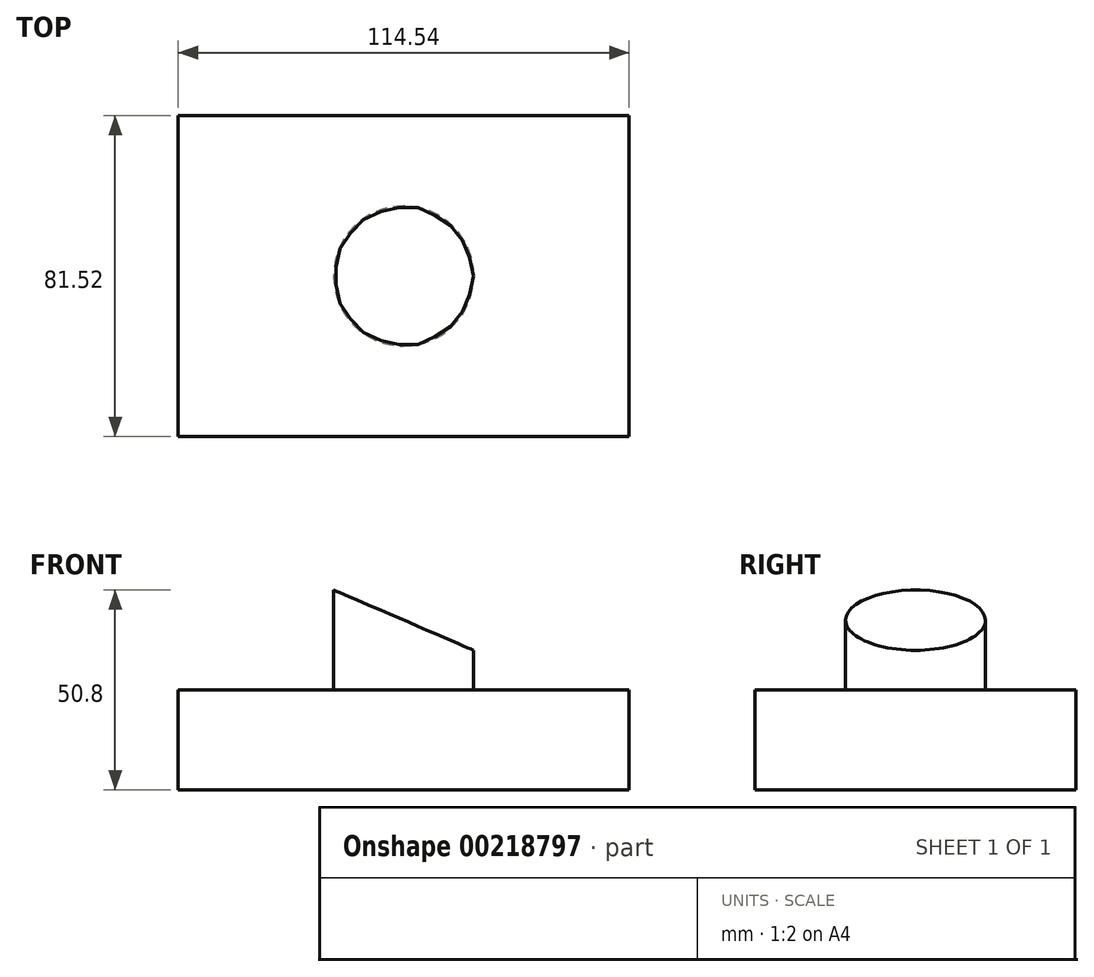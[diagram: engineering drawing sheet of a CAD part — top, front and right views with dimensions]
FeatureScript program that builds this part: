
annotation { "Feature Type Name" : "Feature", "Feature Type Description" : "" }
export const myFeature = defineFeature(function(context is Context, id is Id, definition is map)
    precondition{}
    {
        {
            var Q0;
            Q0=qCreatedBy(makeId("Top.planeOp"),FACE);
            var sketch = newSketch(context, id + "F0", { "sketchPlane" : qUnion([Q0])});
            skLineSegment(sketch, "E0.bottom", {"start": v(57.27, -40.76) * mm, "end": v(-57.27, -40.76) * mm});
            skLineSegment(sketch, "E0.top", {"start": v(57.27, 40.76) * mm, "end": v(-57.27, 40.76) * mm});
            skLineSegment(sketch, "E0.left", {"start": v(57.27, -40.76) * mm, "end": v(57.27, 40.76) * mm});
            skLineSegment(sketch, "E0.right", {"start": v(-57.27, -40.76) * mm, "end": v(-57.27, 40.76) * mm});
            skPoint(sketch, "E0.middle", {"position": v(0, 0) * mm});
            skSolve(sketch);
        }
        {
            var Q0;
            Q0=makeQuery(id+"F0.imprint","IMPRINT",FACE,{"disambiguationData":[TD([[makeQuery(id+"F0.imprint","IMPRINT",EDGE,{"derivedFrom":sQuery(id+"F0.wireOp",EDGE,"E0.bottom")}),-1.0]])]});
            extrude(context, id + "F1", {"entities" : qUnion([Q0]), "depth" : 25.4 * mm});
        }
        {
            var Q0;
            Q0=makeQuery(id+"F1.opExtrude","CAP_FACE",FACE,{"disambiguationData":[OSD([sQuery(id+"F0.wireOp",EDGE,"E0.bottom"),sQuery(id+"F0.wireOp",EDGE,"E0.top"),sQuery(id+"F0.wireOp",EDGE,"E0.left"),sQuery(id+"F0.wireOp",EDGE,"E0.right")])],"isStart":false});
            var sketch = newSketch(context, id + "F2", { "sketchPlane" : qUnion([Q0])});
            skCircle(sketch, "E1", {"center": v(0, 0) * mm, "radius": 17.78 * mm});
            skSolve(sketch);
        }
        {
            var Q0;
            Q0 = qSketchRegion(id + "F2", true);
            extrude(context, id + "F3", {"entities" : qUnion([Q0]), "operationType" : NewBodyOperationType.ADD, "depth" : 25.4 * mm});
        }
        {
            var Q0;
            Q0=qCreatedBy(makeId("Front.planeOp"),FACE);
            var sketch = newSketch(context, id + "F4", { "sketchPlane" : qUnion([Q0])});
            skLineSegment(sketch, "E2.0", {"start": v(-17.78, 50.8) * mm, "end": v(17.78, 50.8) * mm});
            skLineSegment(sketch, "E3", {"start": v(-17.78, 25.4) * mm, "end": v(-17.78, 50.8) * mm});
            skLineSegment(sketch, "E4", {"start": v(17.78, 50.8) * mm, "end": v(17.78, 25.4) * mm});
            skLineSegment(sketch, "E5", {"start": v(-17.78, 50.8) * mm, "end": v(17.78, 35.46) * mm});
            skLineSegment(sketch, "E6", {"start": v(17.78, 35.46) * mm, "end": v(17.78, 50.8) * mm});
            skSolve(sketch);
        }
        {
            var Q0;
            Q0 = qSketchRegion(id + "F4", true);
            extrude(context, id + "F5", {"entities" : qUnion([Q0]), "operationType" : NewBodyOperationType.REMOVE, "endBound" : BoundingType.SYMMETRIC, "depth" : 76.2 * mm});
        }
    });
